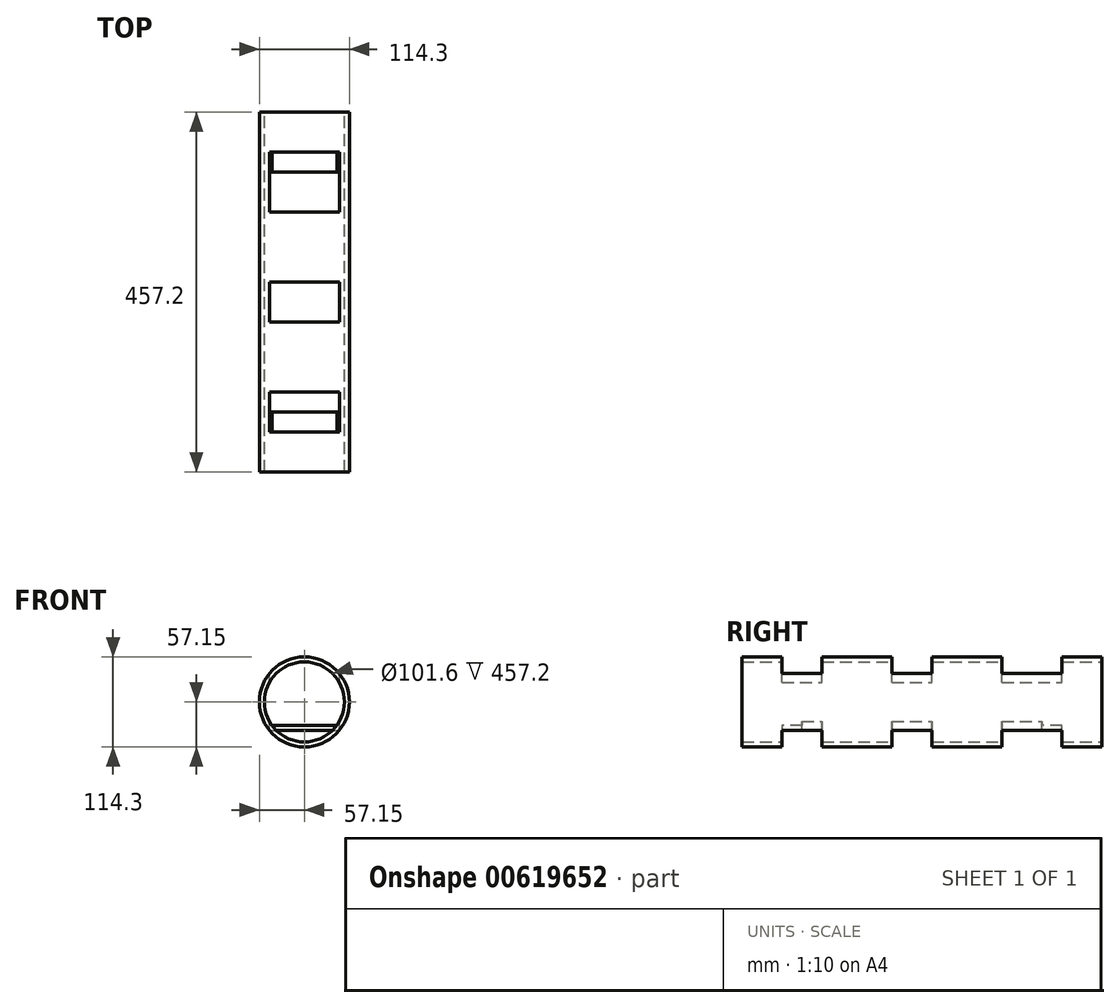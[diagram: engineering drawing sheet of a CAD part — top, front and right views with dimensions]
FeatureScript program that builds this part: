
annotation { "Feature Type Name" : "Feature", "Feature Type Description" : "" }
export const myFeature = defineFeature(function(context is Context, id is Id, definition is map)
    precondition{}
    {
        {
            var Q0;
            Q0=qCreatedBy(makeId("Front.planeOp"),FACE);
            var sketch = newSketch(context, id + "F0", { "sketchPlane" : qUnion([Q0])});
            skPoint(sketch, "E0.middle", {"position": v(0, 0) * mm});
            skCircle(sketch, "E1", {"center": v(0, 0) * mm, "radius": 9.53 * mm});
            skCircle(sketch, "E2", {"center": v(0, 0) * mm, "radius": 57.15 * mm});
            skCircle(sketch, "E3.0", {"center": v(0, 0) * mm, "radius": 50.8 * mm});
            skSolve(sketch);
        }
        {
            var Q0;
            Q0=makeQuery(id+"F0.imprint","IMPRINT",FACE,{"disambiguationData":[TD([[makeQuery(id+"F0.imprint","IMPRINT",EDGE,{"derivedFrom":sQuery(id+"F0.wireOp",EDGE,"E2")}),1.0]])]});
            extrude(context, id + "F1", {"entities" : qUnion([Q0]), "depth" : 457.2 * mm, "offsetDistance" : 25.4 * mm});
        }
        {
            var Q0;
            Q0=qCreatedBy(makeId("Top.planeOp"),FACE);
            var sketch = newSketch(context, id + "F2", { "sketchPlane" : qUnion([Q0])});
            skLineSegment(sketch, "E4", {"start": v(0, -457.2) * mm, "end": v(0, 0) * mm, "construction": true});
            skLineSegment(sketch, "E5", {"start": v(57.15, 0) * mm, "end": v(0, 0) * mm, "construction": true});
            skLineSegment(sketch, "E6.bottom", {"start": v(44.45, -127) * mm, "end": v(-44.45, -127) * mm});
            skLineSegment(sketch, "E6.top", {"start": v(44.45, -76.2) * mm, "end": v(-44.45, -76.2) * mm});
            skLineSegment(sketch, "E6.left", {"start": v(44.45, -156.46) * mm, "end": v(44.45, -127) * mm});
            skLineSegment(sketch, "E6.right", {"start": v(-44.45, -127) * mm, "end": v(-44.45, -101.6) * mm});
            skPoint(sketch, "E6.middle", {"position": v(0, -101.6) * mm});
            skLineSegment(sketch, "E7", {"start": v(44.45, -101.6) * mm, "end": v(-44.45, -101.6) * mm});
            skLineSegment(sketch, "E8", {"start": v(44.45, -156.46) * mm, "end": v(44.45, -76.2) * mm});
            skLineSegment(sketch, "E9", {"start": v(-44.45, -101.6) * mm, "end": v(-44.45, -76.2) * mm});
            skPoint(sketch, "E10.0.1.0", {"position": v(0, -241.3) * mm});
            skLineSegment(sketch, "E10.0.1.1", {"start": v(-44.45, -266.7) * mm, "end": v(-44.45, -241.3) * mm});
            skLineSegment(sketch, "E10.0.1.2", {"start": v(44.45, -266.7) * mm, "end": v(-44.45, -266.7) * mm});
            skLineSegment(sketch, "E10.0.1.3", {"start": v(44.45, -296.16) * mm, "end": v(44.45, -266.7) * mm});
            skLineSegment(sketch, "E10.0.1.4", {"start": v(-44.45, -241.3) * mm, "end": v(-44.45, -215.9) * mm});
            skLineSegment(sketch, "E10.0.1.5", {"start": v(44.45, -215.9) * mm, "end": v(-44.45, -215.9) * mm});
            skLineSegment(sketch, "E10.0.1.6", {"start": v(44.45, -296.16) * mm, "end": v(44.45, -215.9) * mm});
            skLineSegment(sketch, "E10.0.1.7", {"start": v(44.45, -241.3) * mm, "end": v(-44.45, -241.3) * mm});
            skLineSegment(sketch, "E10.direction1", {"start": v(-44.45, -127) * mm, "end": v(-19.05, -127) * mm, "construction": true});
            skLineSegment(sketch, "E10.direction2", {"start": v(-44.45, -127) * mm, "end": v(-44.45, -266.7) * mm, "construction": true});
            skPoint(sketch, "E11.0.0.2", {"position": v(0, -381) * mm});
            skLineSegment(sketch, "E11.1.0.2", {"start": v(-44.45, -406.4) * mm, "end": v(-44.45, -381) * mm});
            skLineSegment(sketch, "E11.4.0.2", {"start": v(44.45, -406.4) * mm, "end": v(-44.45, -406.4) * mm});
            skLineSegment(sketch, "E11.7.0.2", {"start": v(44.45, -435.86) * mm, "end": v(44.45, -406.4) * mm});
            skLineSegment(sketch, "E11.10.0.2", {"start": v(-44.45, -381) * mm, "end": v(-44.45, -355.6) * mm});
            skLineSegment(sketch, "E11.13.0.2", {"start": v(44.45, -355.6) * mm, "end": v(-44.45, -355.6) * mm});
            skLineSegment(sketch, "E11.16.0.2", {"start": v(44.45, -435.86) * mm, "end": v(44.45, -355.6) * mm});
            skLineSegment(sketch, "E11.19.0.2", {"start": v(44.45, -381) * mm, "end": v(-44.45, -381) * mm});
            skLineSegment(sketch, "E12.bottom", {"start": v(-44.45, -76.2) * mm, "end": v(44.45, -76.2) * mm});
            skLineSegment(sketch, "E12.top", {"start": v(-44.45, -50.8) * mm, "end": v(44.45, -50.8) * mm});
            skLineSegment(sketch, "E12.left", {"start": v(-44.45, -76.2) * mm, "end": v(-44.45, -50.8) * mm});
            skLineSegment(sketch, "E12.right", {"start": v(44.45, -76.2) * mm, "end": v(44.45, -50.8) * mm});
            skSolve(sketch);
        }
        {
            var Q0;
            Q0 = qSketchRegion(id + "F2", true);
            var Q1;
            Q1=makeQuery(id+"F1.opExtrude","SWEPT_FACE",FACE,{"disambiguationData":[OSD([sQuery(id+"F0.wireOp",EDGE,"E0.left")])]});
            extrude(context, id + "F3", {"entities" : qUnion([Q0]), "operationType" : NewBodyOperationType.REMOVE, "endBound" : BoundingType.SYMMETRIC, "oppositeDirection" : true, "depth" : 127 * mm, "endBoundEntityFace" : qUnion([Q1]), "offsetDistance" : 25.4 * mm});
        }
        {
            var Q0;
            Q0=makeQuery(id+"F3.boolean.opBoolean","COPY",FACE,{"disambiguationData":[OD(0.0)],"derivedFrom":makeQuery(id+"F3.opExtrude","SWEPT_FACE",FACE,{"disambiguationData":[OSD([sQuery(id+"F2.wireOp",EDGE,"E6.left"),sQuery(id+"F2.wireOp",EDGE,"E8")])]})});
            var Q1;
            Q1=makeQuery(id+"F3.boolean.opBoolean","COPY",FACE,{"disambiguationData":[OD(0.0)],"derivedFrom":makeQuery(id+"F3.opExtrude","SWEPT_FACE",FACE,{"disambiguationData":[OSD([sQuery(id+"F2.wireOp",EDGE,"E11.16.0.2")])]})});
            extrude(context, id + "F4", {"entities" : qUnion([Q0, Q1]), "operationType" : NewBodyOperationType.ADD, "endBound" : BoundingType.UP_TO_NEXT, "depth" : 25.4 * mm, "offsetDistance" : 25.4 * mm});
        }
        {
            var Q0;
            Q0=makeQuery(id+"F2.imprint","IMPRINT",FACE,{"disambiguationData":[TD([[makeQuery(id+"F2.imprint","IMPRINT",EDGE,{"derivedFrom":sQuery(id+"F2.wireOp",EDGE,"E11.10.0.2")}),-1.0]])]});
            var Q1;
            {var subQ0=sQuery(id+"F2.wireOp",EDGE,"E6.bottom");Q1=makeQuery(id+"F2.imprint","IMPRINT",FACE,{"disambiguationData":[TD([[makeQuery(id+"F2.imprint","IMPRINT",EDGE,{"derivedFrom":subQ0}),-1.0]])]});}
            var Q2;
            {var subQ0=sQuery(id+"F2.wireOp",EDGE,"E7");Q2=makeQuery(id+"F2.imprint","IMPRINT",FACE,{"disambiguationData":[TD([[makeQuery(id+"F2.imprint","IMPRINT",EDGE,{"derivedFrom":subQ0}),-1.0]])]});}
            extrude(context, id + "F5", {"entities" : qUnion([Q0, Q1, Q2]), "operationType" : NewBodyOperationType.REMOVE, "endBound" : BoundingType.SYMMETRIC, "oppositeDirection" : true, "depth" : 149.86 * mm, "offsetDistance" : 25.4 * mm});
        }
        {
            var Q0;
            Q0=makeQuery(id+"F4.opExtrude","SWEPT_FACE",FACE,{"disambiguationData":[OSD([sQuery(id+"F2.wireOp",EDGE,"E11.4.0.2"),sQuery(id+"F2.wireOp",EDGE,"E11.16.0.2")])]});
            var sketch = newSketch(context, id + "F6", { "sketchPlane" : qUnion([Q0])});
            skLineSegment(sketch, "E13.bottom", {"start": v(48.9, -24.6) * mm, "end": v(-48.9, -24.6) * mm});
            skLineSegment(sketch, "E13.top", {"start": v(48.9, -29.57) * mm, "end": v(-48.9, -29.57) * mm});
            skLineSegment(sketch, "E13.left", {"start": v(48.9, -29.57) * mm, "end": v(48.9, -24.6) * mm});
            skLineSegment(sketch, "E13.right", {"start": v(-48.9, -29.57) * mm, "end": v(-48.9, -24.6) * mm});
            skSolve(sketch);
        }
        {
            var Q0;
            {var subQ0=sQuery(id+"F6.wireOp",EDGE,"E13.bottom");var subQ1=makeQuery(id+"F1.opExtrude","SWEPT_FACE",FACE,{"disambiguationData":[OSD([sQuery(id+"F0.wireOp",EDGE,"E3.0")])]});var subQ2=sQuery(id+"F2.wireOp",EDGE,"E11.4.0.2");var subQ3=makeQuery(id+"F4.opExtrude","SWEPT_FACE",FACE,{"disambiguationData":[OSD([subQ2,sQuery(id+"F2.wireOp",EDGE,"E11.16.0.2")])]});var subQ4=makeQuery(id+"F3.boolean.opBoolean","INTERSECT",EDGE,{"disambiguationData":[OD(0.0)],"derivedFrom":[subQ1,makeQuery(id+"F3.opExtrude","SWEPT_FACE",FACE,{"disambiguationData":[OSD([subQ2])]})]});var subQ5=makeQuery(id+"F4.boolean.opBoolean","SPLIT",EDGE,{"disambiguationData":[topologyDisambiguationEdgeConnected([subQ1,subQ3]),OD(0.0)],"derivedFrom":subQ4});var subQ6=makeQuery(id+"F6.imprint","INTERSECT",VERTEX,{"derivedFrom":[subQ5,subQ0]});var subQ7=makeQuery(id+"F4.boolean.opBoolean","SPLIT",EDGE,{"disambiguationData":[topologyDisambiguationEdgeConnected([subQ1,subQ3]),OD(1.0)],"derivedFrom":subQ4});var subQ8=makeQuery(id+"F6.imprint","INTERSECT",VERTEX,{"derivedFrom":[subQ7,subQ0]});Q0=makeQuery(id+"F6.imprint","IMPRINT",FACE,{"disambiguationData":[TD([[makeQuery(id+"F6.imprint","IMPRINT",EDGE,{"disambiguationData":[TD([[subQ6,-1.0],[subQ8,1.0]])],"derivedFrom":subQ0}),-1.0]])]});}
            extrude(context, id + "F7", {"entities" : qUnion([Q0]), "operationType" : NewBodyOperationType.REMOVE, "endBound" : BoundingType.THROUGH_ALL, "oppositeDirection" : true, "depth" : 25.4 * mm, "offsetDistance" : 25.4 * mm});
        }
    });
